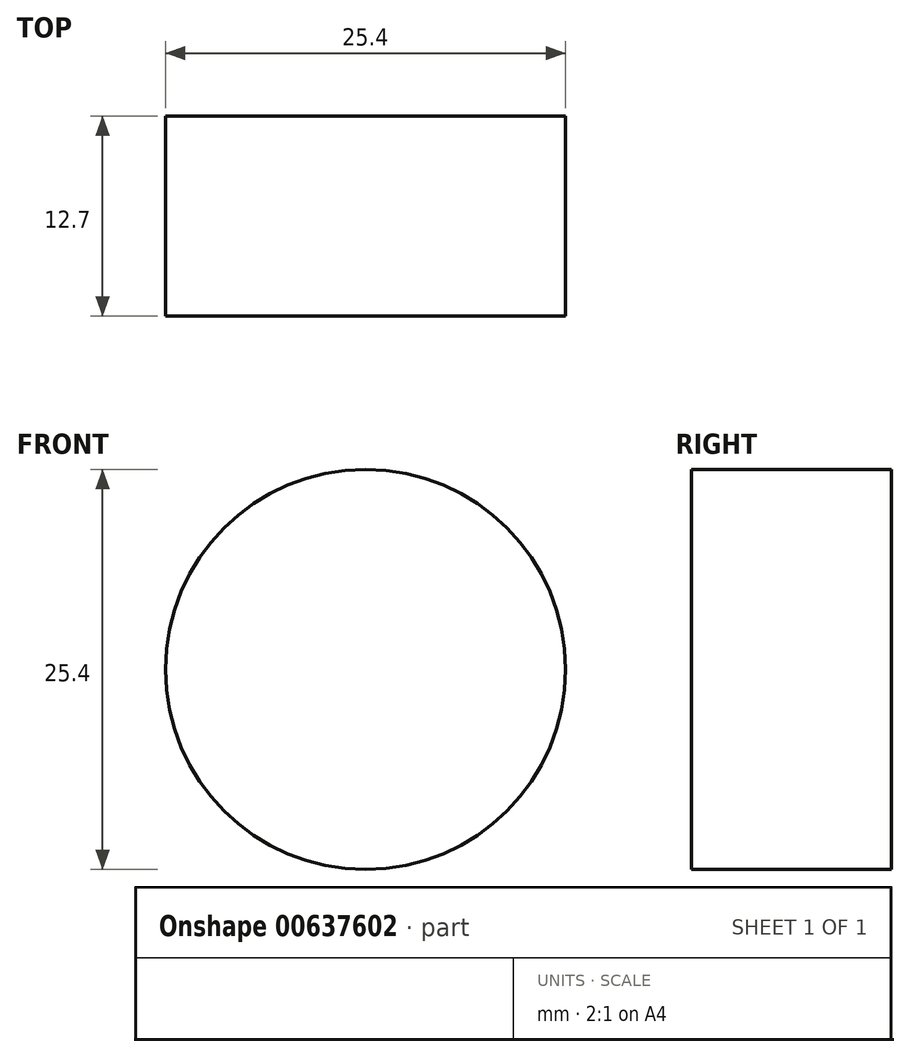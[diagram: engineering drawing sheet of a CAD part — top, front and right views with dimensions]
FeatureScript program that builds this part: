
annotation { "Feature Type Name" : "Feature", "Feature Type Description" : "" }
export const myFeature = defineFeature(function(context is Context, id is Id, definition is map)
    precondition{}
    {
        {
            var Q0;
            Q0=qCreatedBy(makeId("Front.planeOp"),FACE);
            var sketch = newSketch(context, id + "F0", { "sketchPlane" : qUnion([Q0])});
            skCircle(sketch, "E0", {"center": v(0, 0) * mm, "radius": 12.7 * mm});
            skSolve(sketch);
        }
        {
            var Q0;
            Q0=makeQuery(id+"F0.imprint","IMPRINT",FACE,{"disambiguationData":[TD([[makeQuery(id+"F0.imprint","IMPRINT",EDGE,{"derivedFrom":sQuery(id+"F0.wireOp",EDGE,"E0")}),1.0]])]});
            extrude(context, id + "F1", {"entities" : qUnion([Q0]), "depth" : 12.7 * mm, "offsetDistance" : 25.4 * mm});
        }
    });
